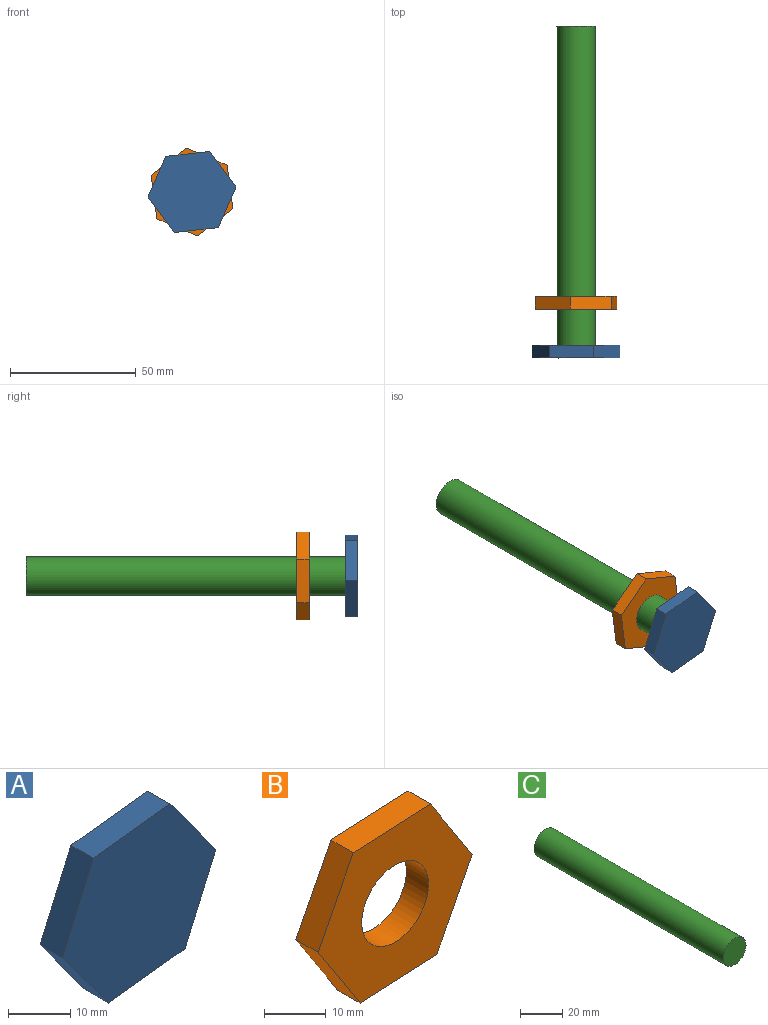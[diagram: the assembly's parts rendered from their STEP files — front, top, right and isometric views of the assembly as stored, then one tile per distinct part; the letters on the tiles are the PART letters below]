
ASSEMBLY  parts=3 mates=2
PART A: 8 faces, bbox 35x5.1x32.3 mm
  f0: plane 17.49x5.08mm, normal (-0.11,0,0.99), area 89.4mm2, adj f1,f5,f6,f7
  f1: plane 16.14x7.02mm, normal (-0.92,0,0.4), area 89.4mm2, adj f0,f2,f6,f7
  f2: plane 14.15x10.46mm, normal (-0.8,0,-0.59), area 89.4mm2, adj f1,f3,f6,f7
  f3: plane 17.49x5.08mm, normal (0.11,0,-0.99), area 89.4mm2, adj f2,f4,f6,f7
  f4: plane 16.14x7.02mm, normal (0.92,0,-0.4), area 89.4mm2, adj f3,f5,f6,f7
  f5: plane 14.15x10.46mm, normal (0.8,0,0.59), area 89.4mm2, adj f0,f4,f6,f7
  f6: plane 34.97x32.27mm, normal (0,-1,0), area 804.6mm2, adj f0,f1,f2,f3,f4,f5
  f7: plane 34.97x32.27mm, normal (0,1,0), area 804.6mm2, adj f0,f1,f2,f3,f4,f5
PART B: 9 faces, bbox 35.1x5.1x31.3 mm
  f0: plane 14.77x9.56mm, normal (0.84,0,0.54), area 89.4mm2, adj f1,f6,f7,f8
  f1: plane 17.58x5.08mm, normal (-0.05,0,1), area 89.4mm2, adj f0,f2,f7,f8
  f2: plane 15.67x8.01mm, normal (-0.89,0,0.46), area 89.4mm2, adj f1,f3,f7,f8
  f3: plane 14.77x9.56mm, normal (-0.84,0,-0.54), area 89.4mm2, adj f2,f4,f7,f8
  f4: plane 17.58x5.08mm, normal (0.05,0,-1), area 89.4mm2, adj f3,f6,f7,f8
  f5: cylinder r=7.62mm len=15.24mm, axis (0,1,0), area 243.2mm2, adj f7,f8
  f6: plane 15.67x8.01mm, normal (0.89,0,-0.46), area 89.4mm2, adj f0,f4,f7,f8
  f7: plane 35.15x31.34mm, normal (0,-1,0), area 622.1mm2, adj f0,f1,f2,f3,f4,f5,f6
  f8: plane 35.15x31.34mm, normal (0,1,0), area 622.1mm2, adj f0,f1,f2,f3,f4,f5,f6
PART C: 3 faces, bbox 15.2x127x15.2 mm
  f0: cylinder r=7.62mm len=127mm, axis (0,1,0), area 6080.5mm2, adj f1,f2
  f1: plane 15.24x15.24mm, normal (0,-1,0), area 182.4mm2, adj f0
  f2: plane 15.24x15.24mm, normal (0,1,0), area 182.4mm2, adj f0
PLACE A t=(175.05,-133.03,130.18)mm
PLACE B rot(axis=(0,1,0),85.5deg) t=(60.82,-113.66,-86.26)mm
PLACE C t=(135.34,-66.99,49.22)mm fixed
MATE fastened C.f0 <-> A.f7  axis (0,1,0) through (28.83,-130.49,63.37)mm
MATE cylindrical C.f0 <-> B.f5  axis (0,1,0) through (28.83,-3.49,63.37)mm
